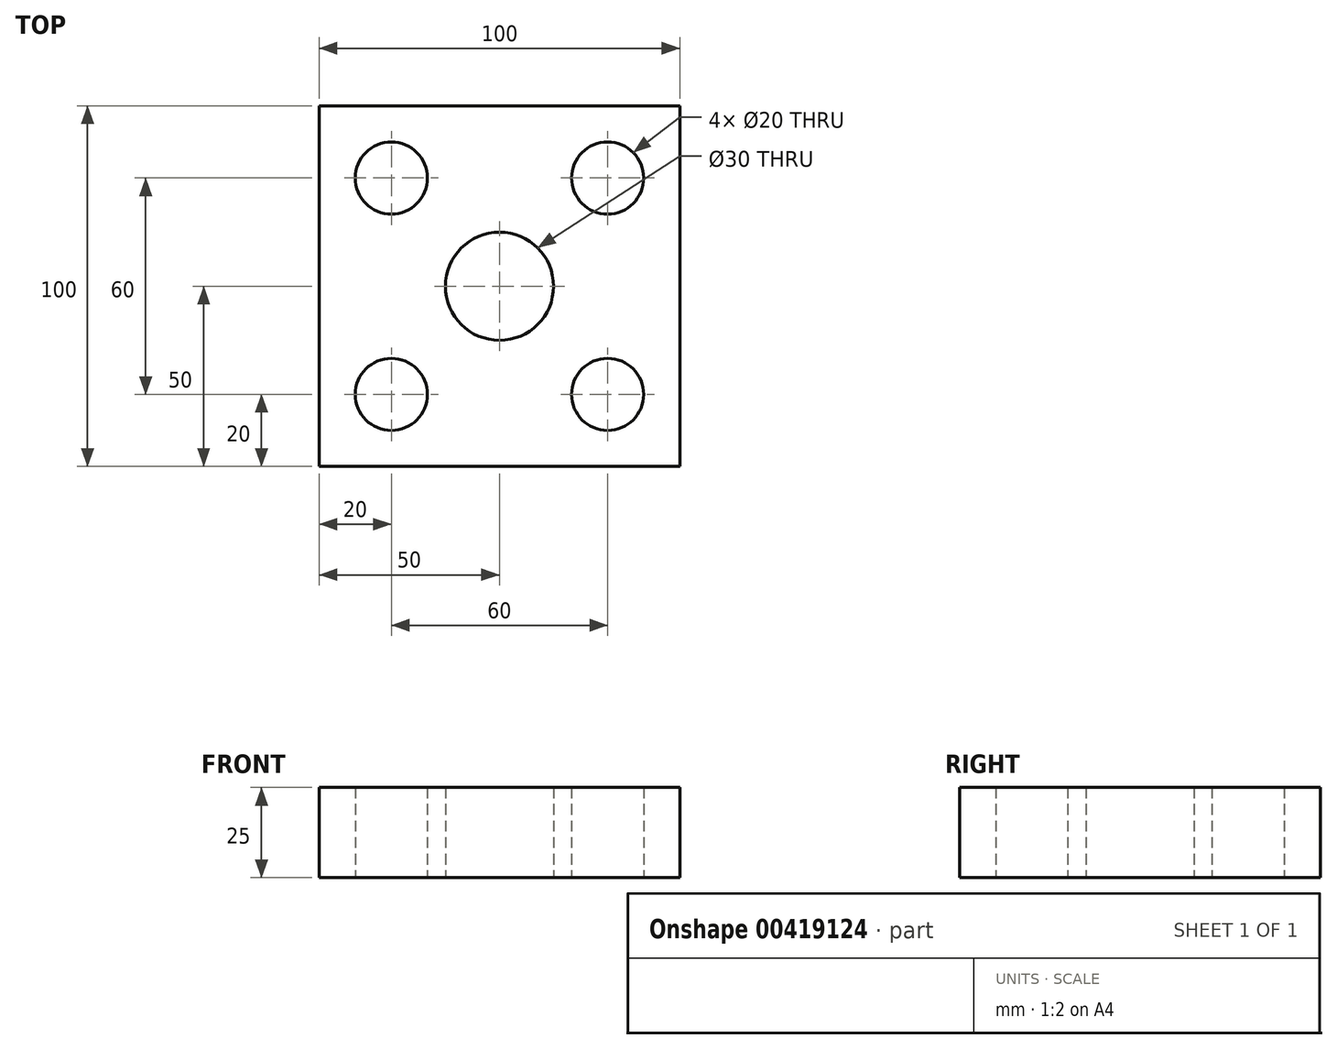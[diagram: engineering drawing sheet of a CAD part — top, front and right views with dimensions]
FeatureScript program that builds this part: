
annotation { "Feature Type Name" : "Feature", "Feature Type Description" : "" }
export const myFeature = defineFeature(function(context is Context, id is Id, definition is map)
    precondition{}
    {
        {
            var Q0;
            Q0=qCreatedBy(makeId("Top.planeOp"),FACE);
            var sketch = newSketch(context, id + "F0", { "sketchPlane" : qUnion([Q0])});
            skLineSegment(sketch, "E0.bottom", {"start": v(50, 50) * mm, "end": v(-50, 50) * mm});
            skLineSegment(sketch, "E0.top", {"start": v(50, -50) * mm, "end": v(-50, -50) * mm});
            skLineSegment(sketch, "E0.left", {"start": v(50, 50) * mm, "end": v(50, -50) * mm});
            skLineSegment(sketch, "E0.right", {"start": v(-50, 50) * mm, "end": v(-50, -50) * mm});
            skPoint(sketch, "E0.middle", {"position": v(0, 0) * mm});
            skCircle(sketch, "E1", {"center": v(0, 0) * mm, "radius": 15 * mm});
            skCircle(sketch, "E2", {"center": v(-30, 30) * mm, "radius": 10 * mm});
            skCircle(sketch, "E3", {"center": v(-30, -30) * mm, "radius": 10 * mm});
            skCircle(sketch, "E4", {"center": v(30, -30) * mm, "radius": 10 * mm});
            skCircle(sketch, "E5", {"center": v(30, 30) * mm, "radius": 10 * mm});
            skSolve(sketch);
        }
        {
            var Q0;
            Q0 = qSketchRegion(id + "F0", true);
            extrude(context, id + "F1", {"entities" : qUnion([Q0]), "depth" : 25 * mm});
        }
    });
